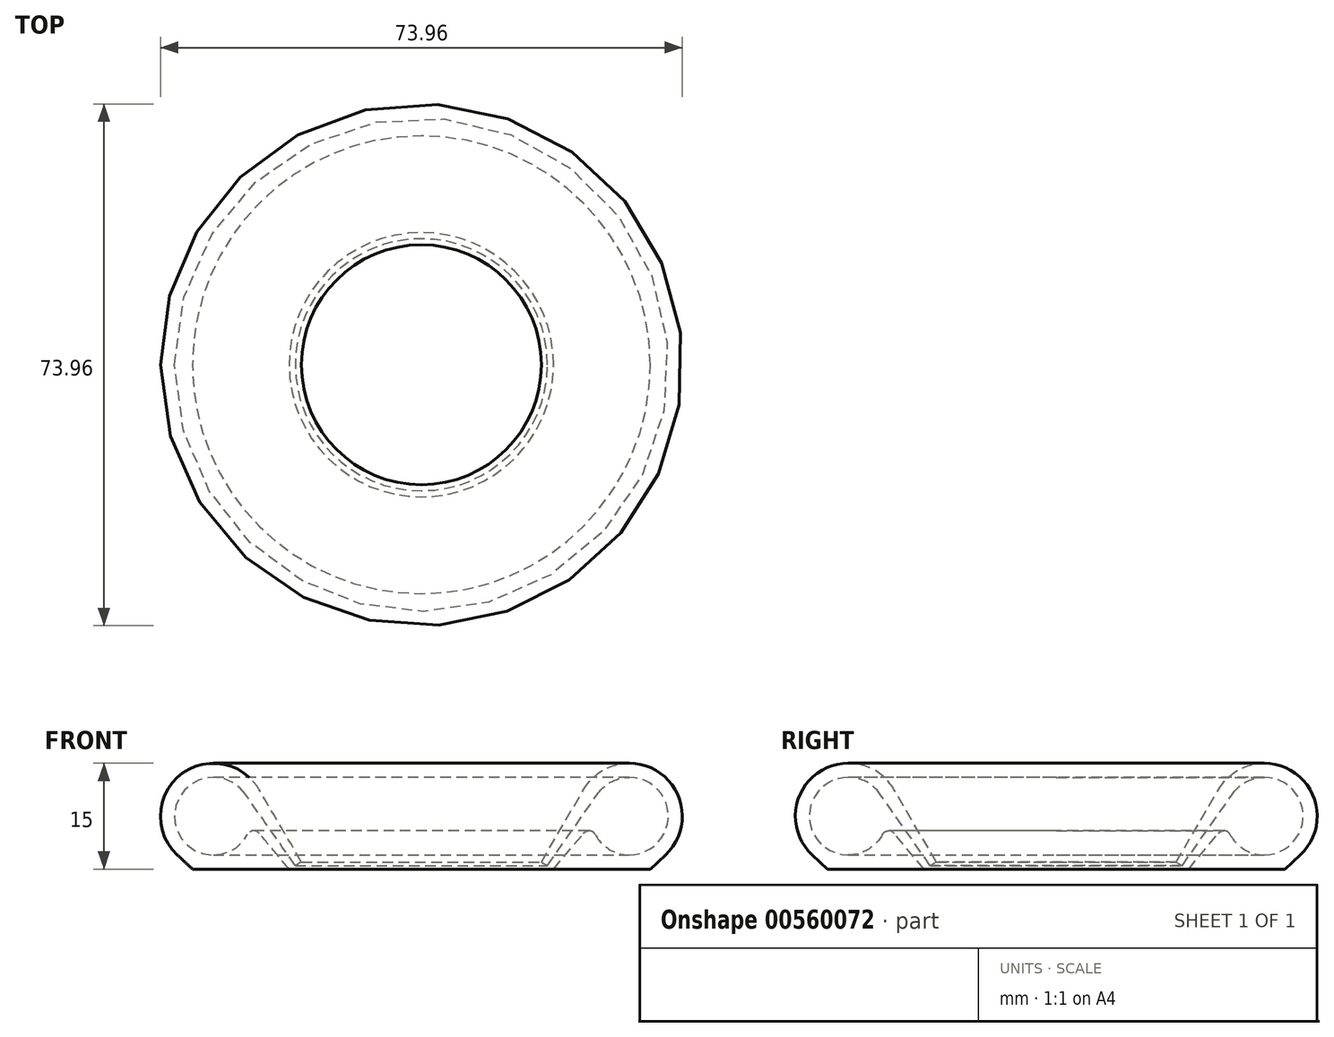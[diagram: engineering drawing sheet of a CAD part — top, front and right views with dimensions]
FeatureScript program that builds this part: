
annotation { "Feature Type Name" : "Feature", "Feature Type Description" : "" }
export const myFeature = defineFeature(function(context is Context, id is Id, definition is map)
    precondition{}
    {
        {
            var Q0;
            Q0=qCreatedBy(makeId("Front.planeOp"),FACE);
            var sketch = newSketch(context, id + "F0", { "sketchPlane" : qUnion([Q0])});
            skLineSegment(sketch, "E0", {"start": v(-18.73, 0) * mm, "end": v(-29.48, 0) * mm});
            skArc(sketch, "E1", {"start": v(-23, 11.28) * mm, "mid": v(-34.16, 13.36) * mm, "end": v(-34.6, 2.01) * mm});
            skArc(sketch, "E2", {"start": v(-24.97, 10.65) * mm, "mid": v(-34.97, 7.17) * mm, "end": v(-24.63, 4.9) * mm});
            skLineSegment(sketch, "E3", {"start": v(-22.98, 5.07) * mm, "end": v(-18.73, 0) * mm});
            skLineSegment(sketch, "E4", {"start": v(-17, 1) * mm, "end": v(-23, 11.28) * mm});
            skLineSegment(sketch, "E5", {"start": v(-24.97, 10.65) * mm, "end": v(-17.86, 0.5) * mm});
            skPoint(sketch, "E6.visualSharp", {"position": v(-24.09, 6.4) * mm});
            skArc(sketch, "E6.filletArc", {"start": v(-22.98, 5.07) * mm, "mid": v(-23.85, 5.42) * mm, "end": v(-24.63, 4.9) * mm});
            skLineSegment(sketch, "E7", {"start": v(-34.6, 2.01) * mm, "end": v(-32.43, 0) * mm});
            skLineSegment(sketch, "E8", {"start": v(-32.43, 0) * mm, "end": v(-29.48, 0) * mm});
            skPoint(sketch, "E9.visualSharp", {"position": v(-18.73, 0) * mm});
            skLineSegment(sketch, "E10", {"start": v(-29.48, 7.5) * mm, "end": v(-29.48, 15) * mm, "construction": true});
            skLineSegment(sketch, "E11", {"start": v(-18.73, 0) * mm, "end": v(-18.73, 0) * mm});
            skLineSegment(sketch, "E12.trimOffspring", {"start": v(-17.86, 0.5) * mm, "end": v(-17, 1) * mm});
            skLineSegment(sketch, "E13", {"start": v(-17.86, 0.5) * mm, "end": v(-18.73, 0) * mm, "construction": true});
            skLineSegment(sketch, "E14", {"start": v(-29.48, 7.5) * mm, "end": v(-36.98, 7.5) * mm, "construction": true});
            skLineSegment(sketch, "E15", {"start": v(0, 0) * mm, "end": v(0, 56.65) * mm, "construction": true});
            skSolve(sketch);
        }
        {
            var Q0;
            Q0=qSketchRegion(id+"F0",true);
            var Q1;
            Q1=sQuery(id+"F0.wireOp",EDGE,"E15");
            revolve(context, id + "F1", {"entities" : qUnion([Q0]), "axis" : qUnion([Q1]), "revolveType" : RevolveType.FULL});
        }
    });
